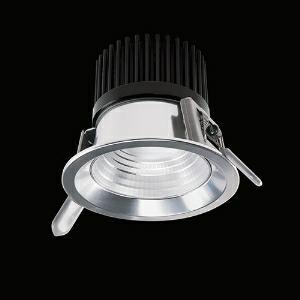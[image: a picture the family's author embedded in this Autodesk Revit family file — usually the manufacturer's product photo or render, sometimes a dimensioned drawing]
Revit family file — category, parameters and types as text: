
# Revit family: spectral_myral_myral_1500-830-s-dali
name_source: partatom
category: Lighting Fixtures
revit_build: Autodesk Revit 2016 (Build: 20150220_1215(x64)
units: mm (PartAtom-declared; Revit-internal decimal feet)

## family parameters
Cut with Voids When Loaded = No
Host = Face
Light Source = No
Part Type = Normal
Room Calculation Point = No
Round Connector Dimension = Use Diameter
Shared = No

## types (1)
- SPECTRAL MYRAL (1 x )
    Apparent Load = 0 VA
    Approval mark = CE
    CIE Flux Codes = 85 100 100 100 100
    Control Gear = Electronic transformer
    Default Elevation = 1800 mm
    Description = SPG0330172
MYRAL recessed spot

Design:
    Height = 0 mm  [stored 0 ft]
    Lamp = 1 x
    Lamp count = 1
    Length = 120 mm
    Luminous efficacy = 0 lm/W
    Manufacturer = Ridi
    ModVariant = No
    Model = MYRAL 1500-830-S-DALI
    Mounting Place = Ceiling
    Mounting Type = Recessed
    Number of Poles = 1
    OnlyDefault = Yes
    Power Factor = 1
    Product Name = SPECTRAL MYRAL
    Product group = Downlight recessed
    ProductGroupID = 400
    Protection Class = Protection class
    Protection Degree = IP 20
    RlxData = <blob elided: 38905 chars, md5=d60c52af>
    Socket = socket
    Standby Power = 0 W
    System Light Flux = 0 lm
    System Power = 0 W
    Type Image = myral_04.jpg
    URL = http://reluxnet.relux.com
    VarID = ---
    Voltage = 0 V
    Weight = 0.00 kg
    Width = 0 mm  [stored 0 ft]

note: [stored X ft] marks values corroborated as IEEE doubles in the binary element streams (Revit-internal decimal feet)

## geometry (parser evidence)
native form markers: Sweep x10
no freeform markers — native parametric forms only
